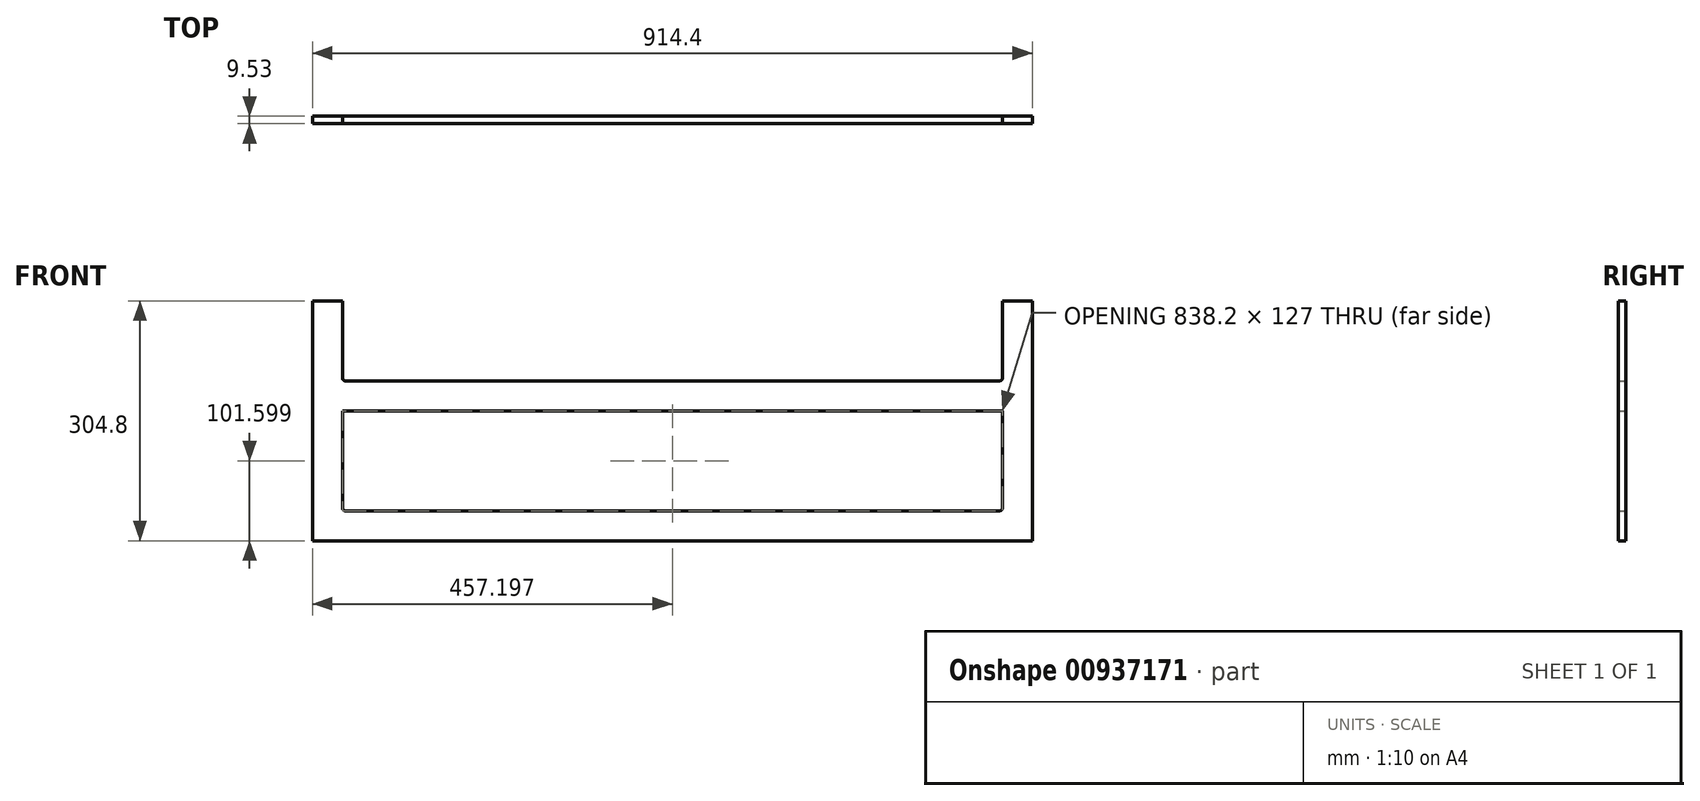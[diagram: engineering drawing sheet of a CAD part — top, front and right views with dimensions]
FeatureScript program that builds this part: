
annotation { "Feature Type Name" : "Feature", "Feature Type Description" : "" }
export const myFeature = defineFeature(function(context is Context, id is Id, definition is map)
    precondition{}
    {
        {
            var Q0;
            Q0=qCreatedBy(makeId("Front.planeOp"),FACE);
            var sketch = newSketch(context, id + "F0", { "sketchPlane" : qUnion([Q0])});
            skLineSegment(sketch, "E0", {"start": v(-525.44, -18.86) * mm, "end": v(-487.34, -18.86) * mm});
            skLineSegment(sketch, "E1", {"start": v(-487.34, -18.86) * mm, "end": v(-487.34, -120.46) * mm});
            skLineSegment(sketch, "E2", {"start": v(-487.34, -120.46) * mm, "end": v(350.86, -120.46) * mm});
            skLineSegment(sketch, "E3", {"start": v(350.86, -120.46) * mm, "end": v(350.86, -18.86) * mm});
            skLineSegment(sketch, "E4", {"start": v(350.86, -18.86) * mm, "end": v(388.96, -18.86) * mm});
            skLineSegment(sketch, "E5", {"start": v(388.96, -18.86) * mm, "end": v(388.96, -323.66) * mm});
            skLineSegment(sketch, "E6", {"start": v(388.96, -323.66) * mm, "end": v(-525.44, -323.66) * mm});
            skLineSegment(sketch, "E7", {"start": v(-525.44, -323.66) * mm, "end": v(-525.44, -18.86) * mm});
            skLineSegment(sketch, "E8.bottom", {"start": v(-487.34, -158.56) * mm, "end": v(350.86, -158.56) * mm});
            skLineSegment(sketch, "E8.top", {"start": v(-487.34, -285.56) * mm, "end": v(350.86, -285.56) * mm});
            skLineSegment(sketch, "E8.left", {"start": v(-487.34, -158.56) * mm, "end": v(-487.34, -285.56) * mm});
            skLineSegment(sketch, "E8.right", {"start": v(350.86, -158.56) * mm, "end": v(350.86, -285.56) * mm});
            skSolve(sketch);
        }
        {
            var Q0;
            Q0=makeQuery(id+"F0.imprint","IMPRINT",FACE,{"disambiguationData":[TD([[makeQuery(id+"F0.imprint","IMPRINT",EDGE,{"derivedFrom":sQuery(id+"F0.wireOp",EDGE,"E0")}),-1.0]])]});
            extrude(context, id + "F1", {"entities" : qUnion([Q0]), "depth" : 9.52 * mm, "offsetDistance" : 25.4 * mm});
        }
        {
            var Q0;
            Q0=makeQuery(id+"F1.opExtrude","SWEPT_EDGE",EDGE,{"disambiguationData":[OSD([sQuery(id+"F0.wireOp",EDGE,"E8.top"),sQuery(id+"F0.wireOp",EDGE,"E8.left")])]});
            var Q1;
            Q1=makeQuery(id+"F1.opExtrude","SWEPT_EDGE",EDGE,{"disambiguationData":[OSD([sQuery(id+"F0.wireOp",EDGE,"E8.top"),sQuery(id+"F0.wireOp",EDGE,"E8.right")])]});
            var Q2;
            Q2=makeQuery(id+"F1.opExtrude","SWEPT_EDGE",EDGE,{"disambiguationData":[OSD([sQuery(id+"F0.wireOp",EDGE,"E2"),sQuery(id+"F0.wireOp",EDGE,"E3")])]});
            var Q3;
            Q3=makeQuery(id+"F1.opExtrude","SWEPT_EDGE",EDGE,{"disambiguationData":[OSD([sQuery(id+"F0.wireOp",EDGE,"E1"),sQuery(id+"F0.wireOp",EDGE,"E2")])]});
            fillet(context, id + "F2", {"entities" : qUnion([Q0, Q1, Q2, Q3]), "radius" : 3.17 * mm, "tangentPropagation" : true, "allowEdgeOverflow" : false});
        }
    });
